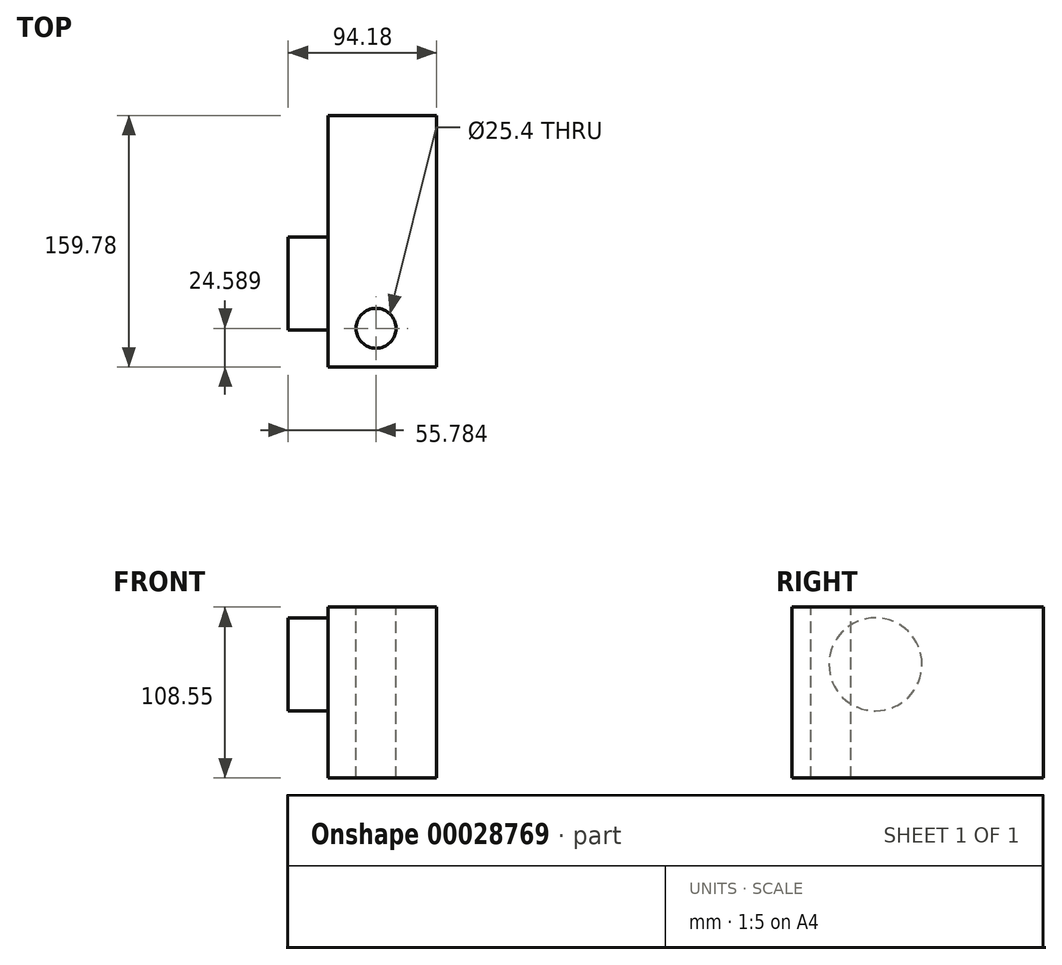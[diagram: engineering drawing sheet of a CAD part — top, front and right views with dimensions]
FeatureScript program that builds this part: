
annotation { "Feature Type Name" : "Feature", "Feature Type Description" : "" }
export const myFeature = defineFeature(function(context is Context, id is Id, definition is map)
    precondition{}
    {
        {
            var Q0;
            Q0=qCreatedBy(makeId("Front.planeOp"),FACE);
            var sketch = newSketch(context, id + "F0", { "sketchPlane" : qUnion([Q0])});
            skLineSegment(sketch, "E0.bottom", {"start": v(27.66, -44.72) * mm, "end": v(-41.12, -44.72) * mm});
            skLineSegment(sketch, "E0.top", {"start": v(27.66, 63.83) * mm, "end": v(-41.12, 63.83) * mm});
            skLineSegment(sketch, "E0.left", {"start": v(27.66, -44.72) * mm, "end": v(27.66, 63.83) * mm});
            skLineSegment(sketch, "E0.right", {"start": v(-41.12, -44.72) * mm, "end": v(-41.12, 63.83) * mm});
            skSolve(sketch);
        }
        {
            var Q0;
            Q0=makeQuery(id+"F0.imprint","IMPRINT",FACE,{"disambiguationData":[TD([[makeQuery(id+"F0.imprint","IMPRINT",EDGE,{"derivedFrom":sQuery(id+"F0.wireOp",EDGE,"E0.bottom")}),-1.0]])]});
            extrude(context, id + "F1", {"entities" : qUnion([Q0]), "depth" : 159.78 * mm});
        }
        {
            var Q0;
            Q0=makeQuery(id+"F1.opExtrude","SWEPT_FACE",FACE,{"disambiguationData":[OSD([sQuery(id+"F0.wireOp",EDGE,"E0.right")])]});
            var sketch = newSketch(context, id + "F2", { "sketchPlane" : qUnion([Q0])});
            skCircle(sketch, "E1", {"center": v(106.76, 27.48) * mm, "radius": 29.5 * mm});
            skSolve(sketch);
        }
        {
            var Q0;
            Q0=makeQuery(id+"F2.imprint","IMPRINT",FACE,{"disambiguationData":[TD([[makeQuery(id+"F2.imprint","IMPRINT",EDGE,{"derivedFrom":sQuery(id+"F2.wireOp",EDGE,"E1")}),1.0]])]});
            extrude(context, id + "F6", {"entities" : qUnion([Q0]), "operationType" : NewBodyOperationType.ADD, "depth" : 25.4 * mm});
        }
        {
            var Q0;
            Q0=makeQuery(id+"F1.opExtrude","SWEPT_FACE",FACE,{"disambiguationData":[OSD([sQuery(id+"F0.wireOp",EDGE,"E0.top")])]});
            var sketch = newSketch(context, id + "F3", { "sketchPlane" : qUnion([Q0])});
            skSolve(sketch);
        }
        {
            var Q0;
            {var subQ0=sQuery(id+"F0.wireOp",EDGE,"E0.top");Q0=makeQuery(id+"F3.imprint","IMPRINT",FACE,{"disambiguationData":[TD([[makeQuery(id+"F3.imprint","IMPRINT",EDGE,{"derivedFrom":makeQuery(id+"F1.opExtrude","CAP_EDGE",EDGE,{"disambiguationData":[OSD([subQ0])],"isStart":true})}),1.0]])]});}
            var sketch = newSketch(context, id + "F4", { "sketchPlane" : qUnion([Q0])});
            skCircle(sketch, "E2", {"center": v(-10.74, -135.2) * mm, "radius": 16.56 * mm});
            skSolve(sketch);
        }
        {
            var Q0;
            Q0=sQuery(id+"F4.wireOp",VERTEX,"E2.center");
            var Q1;
            Q1=makeQuery(id+"F1.opExtrude","SWEPT_BODY",BODY,{"disambiguationData":[OSD([sQuery(id+"F0.wireOp",EDGE,"E0.bottom"),sQuery(id+"F0.wireOp",EDGE,"E0.top"),sQuery(id+"F0.wireOp",EDGE,"E0.left"),sQuery(id+"F0.wireOp",EDGE,"E0.right")])]});
            hole(context, id + "F5", {"style" : HoleStyle.SIMPLE, "holeDiameter" : 25.4 * mm, "endStyle" : HoleEndStyle.THROUGH, "locations" : qUnion([Q0]), "scope" : qUnion([Q1])});
        }
    });
